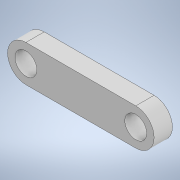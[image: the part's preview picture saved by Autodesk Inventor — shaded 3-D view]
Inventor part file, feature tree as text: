
AUTODESK INVENTOR PART (.ipt)
format: ipt  version: 2022 (Build 260153000, 153)  size: 107,008 bytes
history: native  units: mm
features: extrude x1, sketch x1
ambient origin geometry x8: Origin, YZ Plane, XZ Plane, XY Plane, X Axis, Y Axis, Z Axis, Center Point
bodies: Solid1 (feature_tree)
feature tree (2):
  extrude  "Extrusion1"  Depth=5.0mm
  sketch  "Sketch1"  dims[d0=10.0mm d3=5.0mm d4=0.0mm d5=30.0mm d6=6.0mm]
